# Revit family: 17.2  Канальный осевой вентилятор FE Тип С
name_source: partatom
category: Оборудование
revit_build: Autodesk Revit 2016 (Build: 20151209_0715(x64)
units: mm (PartAtom-declared; Revit-internal decimal feet)

## family parameters
Всегда вертикально = Да
На основе рабочей плоскости = Нет
Общий = Нет
При загрузке вырезать с полостями = Нет
Размер круглого соединителя = Использовать диаметр
Тип детали = Нормальный
Точка расчета площади = Нет

## types (3) — shared parameters
Единица измерения = шт.
Завод изготовитель = KORF
И = 72 мм
И1 = 130 мм
И2 = 65 мм
Ключевая пометка = Вентиляция
Материал = Сталь серая
Наименование и тех.хар-ка = Канальный осевой вентилятор
Раздел = ОВ
Размер В = 12 мм

## per-type parameters (varying)
| type | А | А! | Б | Г | Г1 | Д | Д1 | Д2 | Д3 | Ж | Масса единицы | Мощность, кВт | Сила тока J, А | Тип, марка, обозначение | Частота вращения n, об/мин | х |
| FE071-SDF | 751 мм | 376 мм | 16 мм | 785 мм | 393 мм | 711 мм | 356 мм | 107 мм | 78 мм | 260 мм | 31 кг | 1 Вт | 1.75 | FE071-SDF.6F.V7 | 900 | 107 мм |
| FE071-ADF | 751 мм | 376 мм | 16 мм | 785 мм | 393 мм | 711 мм | 356 мм | 107 мм | 78 мм | 260 мм | 31 кг | 0 Вт | 0.94 | FE071-ADF.6F.V7 | 680 | 107 мм |
| FE080-SDF | 837 мм | 419 мм | 24 мм | 871 мм | 436 мм | 797 мм | 399 мм | 120 мм | 88 мм | 280 мм | 46 кг | 2 Вт | 1 | FE080-SDF.6N.V7 | 880 | 120 мм |
